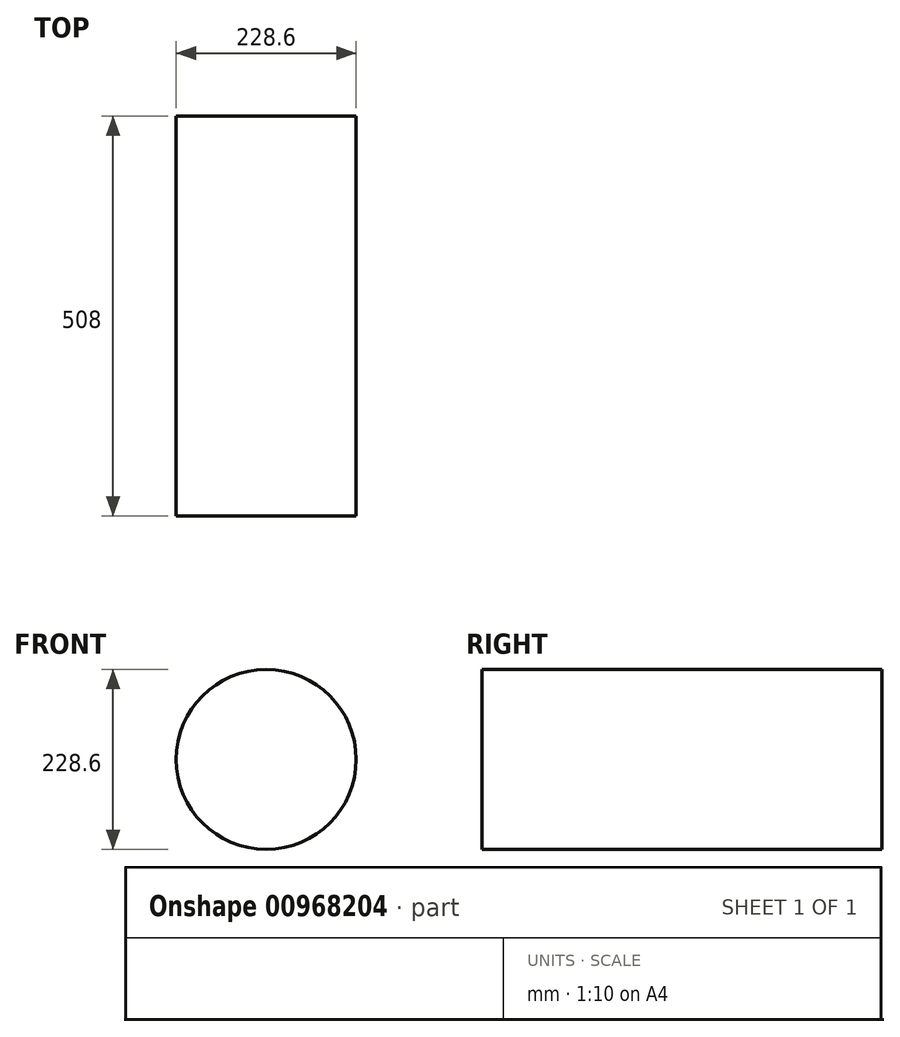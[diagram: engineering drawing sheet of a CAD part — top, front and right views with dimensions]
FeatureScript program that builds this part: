
annotation { "Feature Type Name" : "Feature", "Feature Type Description" : "" }
export const myFeature = defineFeature(function(context is Context, id is Id, definition is map)
    precondition{}
    {
        {
            var Q0;
            Q0=qCreatedBy(makeId("Front.planeOp"),FACE);
            var sketch = newSketch(context, id + "F0", { "sketchPlane" : qUnion([Q0])});
            skCircle(sketch, "E0", {"center": v(0, 0) * mm, "radius": 114.3 * mm});
            skSolve(sketch);
        }
        {
            var Q0;
            Q0 = qSketchRegion(id + "F0", true);
            extrude(context, id + "F1", {"entities" : qUnion([Q0]), "depth" : 508 * mm, "offsetDistance" : 25.4 * mm});
        }
    });
